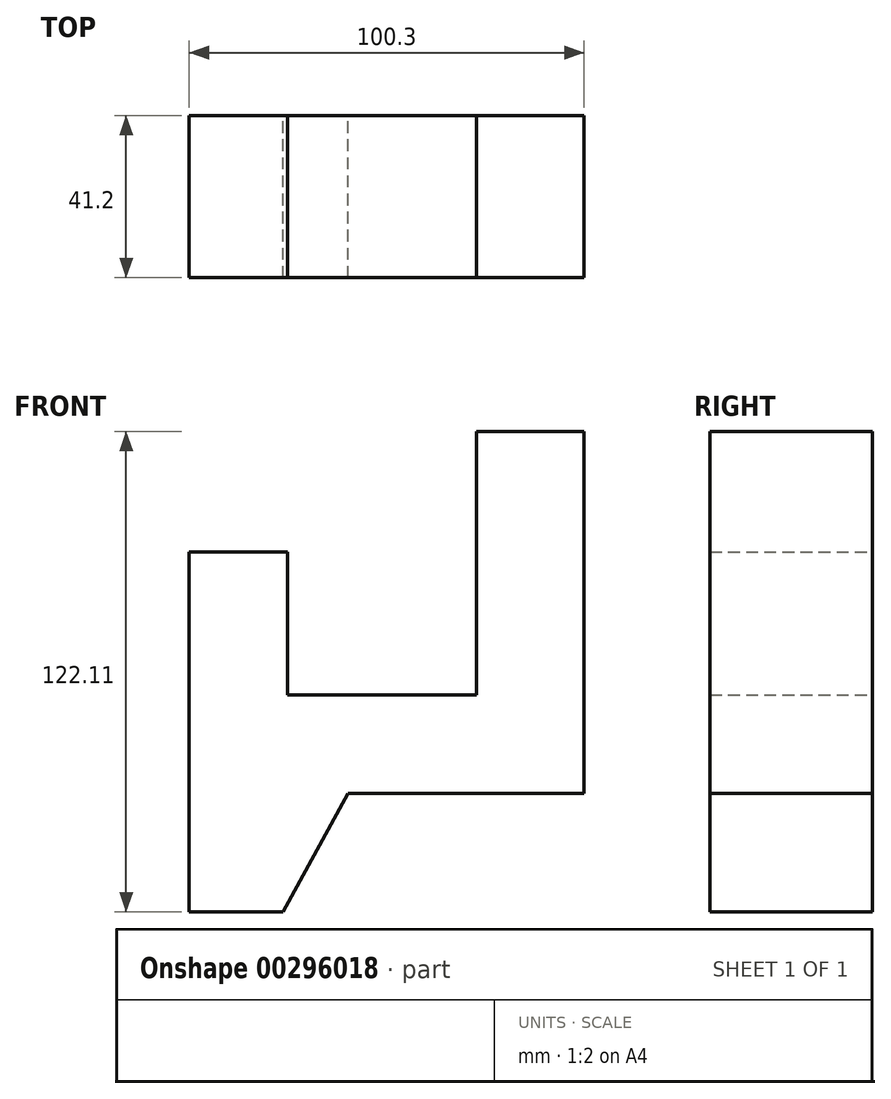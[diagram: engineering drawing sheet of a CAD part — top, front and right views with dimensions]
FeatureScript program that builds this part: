
annotation { "Feature Type Name" : "Feature", "Feature Type Description" : "" }
export const myFeature = defineFeature(function(context is Context, id is Id, definition is map)
    precondition{}
    {
        {
            var Q0;
            Q0=qCreatedBy(makeId("Front.planeOp"),FACE);
            var sketch = newSketch(context, id + "F0", { "sketchPlane" : qUnion([Q0])});
            skLineSegment(sketch, "E0", {"start": v(-80.6, -76.1) * mm, "end": v(-80.6, 15.3) * mm});
            skLineSegment(sketch, "E1", {"start": v(-80.6, 15.3) * mm, "end": v(-55.6, 15.3) * mm});
            skLineSegment(sketch, "E2", {"start": v(-55.6, 15.3) * mm, "end": v(-55.6, -20.99) * mm});
            skLineSegment(sketch, "E3", {"start": v(-55.6, -20.99) * mm, "end": v(-7.6, -20.99) * mm});
            skLineSegment(sketch, "E4", {"start": v(-7.6, -20.99) * mm, "end": v(-7.6, 46.01) * mm});
            skLineSegment(sketch, "E5", {"start": v(-7.6, 46.01) * mm, "end": v(19.7, 46.01) * mm});
            skLineSegment(sketch, "E6", {"start": v(19.7, 46.01) * mm, "end": v(19.7, -45.99) * mm});
            skLineSegment(sketch, "E7", {"start": v(19.7, -45.99) * mm, "end": v(-40.3, -45.99) * mm});
            skLineSegment(sketch, "E8", {"start": v(-40.3, -45.99) * mm, "end": v(-56.8, -76.1) * mm});
            skLineSegment(sketch, "E9", {"start": v(-56.8, -76.1) * mm, "end": v(-80.6, -76.1) * mm});
            skSolve(sketch);
        }
        {
            var Q0;
            Q0=makeQuery(id+"F0.imprint","IMPRINT",FACE,{"disambiguationData":[TD([[makeQuery(id+"F0.imprint","IMPRINT",EDGE,{"derivedFrom":sQuery(id+"F0.wireOp",EDGE,"E0")}),-1.0]])]});
            extrude(context, id + "F1", {"entities" : qUnion([Q0]), "depth" : 41.2 * mm});
        }
    });
